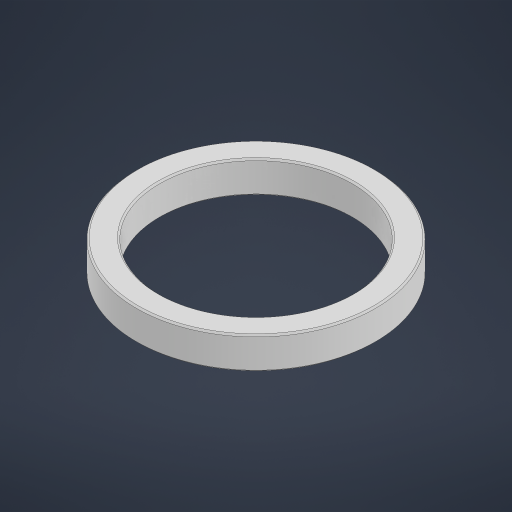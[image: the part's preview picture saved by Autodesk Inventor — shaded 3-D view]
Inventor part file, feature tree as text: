
AUTODESK INVENTOR PART (.ipt)
format: ipt  version: 2023 (Build 270158000, 158)  size: 192,512 bytes
history: native  units: in
note: dims shown in document units (in); Inventor stores cm internally (conversion verified against a paired STEP export)
features: chamfer x1
ambient origin geometry x8: Origin, YZ Plane, XZ Plane, XY Plane, X Axis, Y Axis, Z Axis, Center Point
bodies: Solid1 (feature_tree)
feature tree (1):
  chamfer  "Chamfer1"  [1 undecoded]
note: 1 required parameter value undecoded (feature->parameter linkage not recoverable at this tier; creation-order binding heuristic only, values carry confidence <= 0.55)
